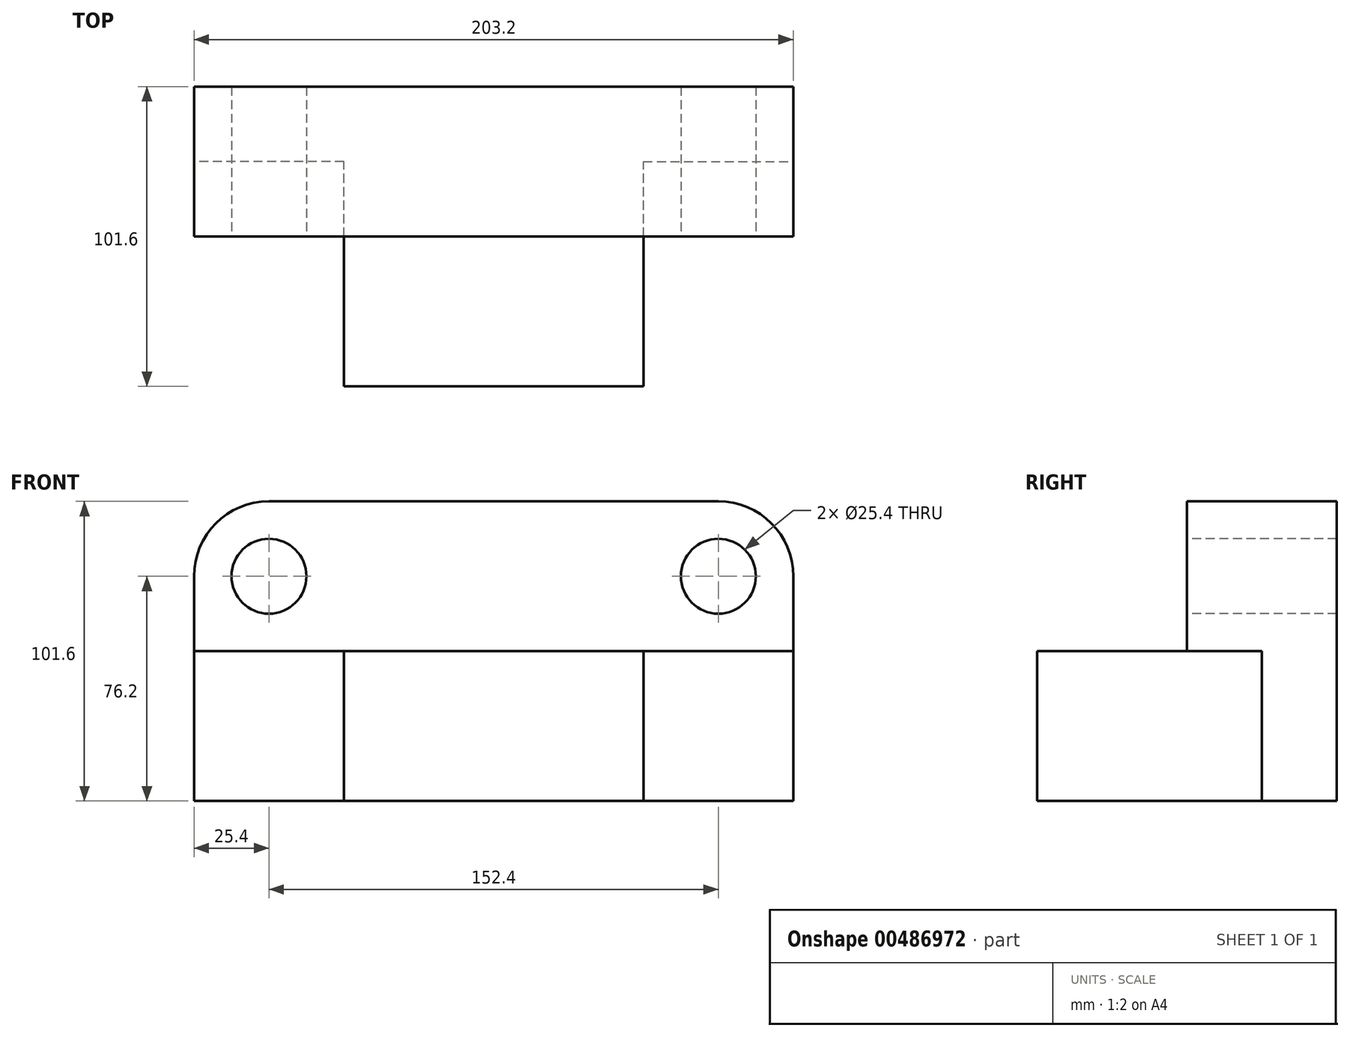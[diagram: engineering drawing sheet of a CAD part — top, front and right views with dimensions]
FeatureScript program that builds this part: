
annotation { "Feature Type Name" : "Feature", "Feature Type Description" : "" }
export const myFeature = defineFeature(function(context is Context, id is Id, definition is map)
    precondition{}
    {
        {
            var Q0;
            Q0=qCreatedBy(makeId("Front.planeOp"),FACE);
            var sketch = newSketch(context, id + "F0", { "sketchPlane" : qUnion([Q0])});
            skLineSegment(sketch, "E0.bottom", {"start": v(0, 0) * mm, "end": v(-203.2, 0) * mm});
            skLineSegment(sketch, "E0.top", {"start": v(-25.4, 101.6) * mm, "end": v(-177.8, 101.6) * mm});
            skLineSegment(sketch, "E0.left", {"start": v(0, 0) * mm, "end": v(0, 76.2) * mm});
            skLineSegment(sketch, "E0.right", {"start": v(-203.2, 0) * mm, "end": v(-203.2, 76.2) * mm});
            skLineSegment(sketch, "E1", {"start": v(-203.2, 76.2) * mm, "end": v(-177.8, 76.2) * mm});
            skArc(sketch, "E2", {"start": v(-177.8, 101.6) * mm, "mid": v(-195.76, 94.16) * mm, "end": v(-203.2, 76.2) * mm});
            skLineSegment(sketch, "E3", {"start": v(0, 76.2) * mm, "end": v(-25.4, 76.2) * mm});
            skArc(sketch, "E4", {"start": v(0, 76.2) * mm, "mid": v(-7.44, 94.16) * mm, "end": v(-25.4, 101.6) * mm});
            skSolve(sketch);
        }
        {
            var Q0;
            Q0=makeQuery(id+"F0.imprint","IMPRINT",FACE,{"disambiguationData":[TD([[makeQuery(id+"F0.imprint","IMPRINT",EDGE,{"derivedFrom":sQuery(id+"F0.wireOp",EDGE,"E0.bottom")}),-1.0]])]});
            extrude(context, id + "F1", {"entities" : qUnion([Q0]), "depth" : 50.8 * mm});
        }
        {
            var Q0;
            Q0=makeQuery(id+"F1.opExtrude","CAP_FACE",FACE,{"disambiguationData":[OSD([sQuery(id+"F0.wireOp",EDGE,"E0.bottom"),sQuery(id+"F0.wireOp",EDGE,"E0.top"),sQuery(id+"F0.wireOp",EDGE,"E0.left"),sQuery(id+"F0.wireOp",EDGE,"E0.right"),sQuery(id+"F0.wireOp",EDGE,"E2"),sQuery(id+"F0.wireOp",EDGE,"E4")])],"isStart":false});
            var sketch = newSketch(context, id + "F2", { "sketchPlane" : qUnion([Q0])});
            skLineSegment(sketch, "E5.bottom", {"start": v(-203.2, 0) * mm, "end": v(0, 0) * mm});
            skLineSegment(sketch, "E5.top", {"start": v(-203.2, 50.8) * mm, "end": v(0, 50.8) * mm});
            skLineSegment(sketch, "E5.left", {"start": v(-203.2, 0) * mm, "end": v(-203.2, 50.8) * mm});
            skLineSegment(sketch, "E5.right", {"start": v(0, 0) * mm, "end": v(0, 50.8) * mm});
            skSolve(sketch);
        }
        {
            var Q0;
            Q0=makeQuery(id+"F2.imprint","IMPRINT",FACE,{"disambiguationData":[TD([[makeQuery(id+"F2.imprint","IMPRINT",EDGE,{"derivedFrom":sQuery(id+"F2.wireOp",EDGE,"E5.bottom")}),-1.0]])]});
            extrude(context, id + "F3", {"entities" : qUnion([Q0]), "operationType" : NewBodyOperationType.REMOVE, "oppositeDirection" : true, "depth" : 25.4 * mm});
        }
        {
            var Q0;
            Q0=makeQuery(id+"F3.boolean.opBoolean","COPY",FACE,{"derivedFrom":makeQuery(id+"F3.opExtrude","CAP_FACE",FACE,{"disambiguationData":[OSD([sQuery(id+"F2.wireOp",EDGE,"E5.bottom"),sQuery(id+"F2.wireOp",EDGE,"E5.top"),sQuery(id+"F2.wireOp",EDGE,"E5.left"),sQuery(id+"F2.wireOp",EDGE,"E5.right")])],"isStart":false})});
            var sketch = newSketch(context, id + "F4", { "sketchPlane" : qUnion([Q0])});
            skLineSegment(sketch, "E6.bottom", {"start": v(-152.4, 50.8) * mm, "end": v(-50.8, 50.8) * mm});
            skLineSegment(sketch, "E6.top", {"start": v(-152.4, 0) * mm, "end": v(-50.8, 0) * mm});
            skLineSegment(sketch, "E6.left", {"start": v(-152.4, 50.8) * mm, "end": v(-152.4, 0) * mm});
            skLineSegment(sketch, "E6.right", {"start": v(-50.8, 50.8) * mm, "end": v(-50.8, 0) * mm});
            skSolve(sketch);
        }
        {
            var Q0;
            Q0=makeQuery(id+"F4.imprint","IMPRINT",FACE,{"disambiguationData":[TD([[makeQuery(id+"F4.imprint","IMPRINT",EDGE,{"derivedFrom":sQuery(id+"F4.wireOp",EDGE,"E6.bottom")}),-1.0]])]});
            extrude(context, id + "F5", {"entities" : qUnion([Q0]), "operationType" : NewBodyOperationType.ADD, "depth" : 76.2 * mm});
        }
        {
            var Q0;
            Q0=makeQuery(id+"F1.opExtrude","CAP_FACE",FACE,{"disambiguationData":[OSD([sQuery(id+"F0.wireOp",EDGE,"E0.bottom"),sQuery(id+"F0.wireOp",EDGE,"E0.top"),sQuery(id+"F0.wireOp",EDGE,"E0.left"),sQuery(id+"F0.wireOp",EDGE,"E0.right"),sQuery(id+"F0.wireOp",EDGE,"E2"),sQuery(id+"F0.wireOp",EDGE,"E4")])],"isStart":false});
            var sketch = newSketch(context, id + "F6", { "sketchPlane" : qUnion([Q0])});
            skCircle(sketch, "E7", {"center": v(-25.4, 76.2) * mm, "radius": 12.7 * mm});
            skCircle(sketch, "E8", {"center": v(-177.8, 76.2) * mm, "radius": 12.7 * mm});
            skSolve(sketch);
        }
        {
            var Q0;
            Q0=makeQuery(id+"F6.imprint","IMPRINT",FACE,{"disambiguationData":[TD([[makeQuery(id+"F6.imprint","IMPRINT",EDGE,{"derivedFrom":sQuery(id+"F6.wireOp",EDGE,"E8")}),1.0]])]});
            var Q1;
            Q1=makeQuery(id+"F6.imprint","IMPRINT",FACE,{"disambiguationData":[TD([[makeQuery(id+"F6.imprint","IMPRINT",EDGE,{"derivedFrom":sQuery(id+"F6.wireOp",EDGE,"E7")}),1.0]])]});
            extrude(context, id + "F7", {"entities" : qUnion([Q0, Q1]), "operationType" : NewBodyOperationType.REMOVE, "oppositeDirection" : true, "depth" : 50.8 * mm});
        }
    });
